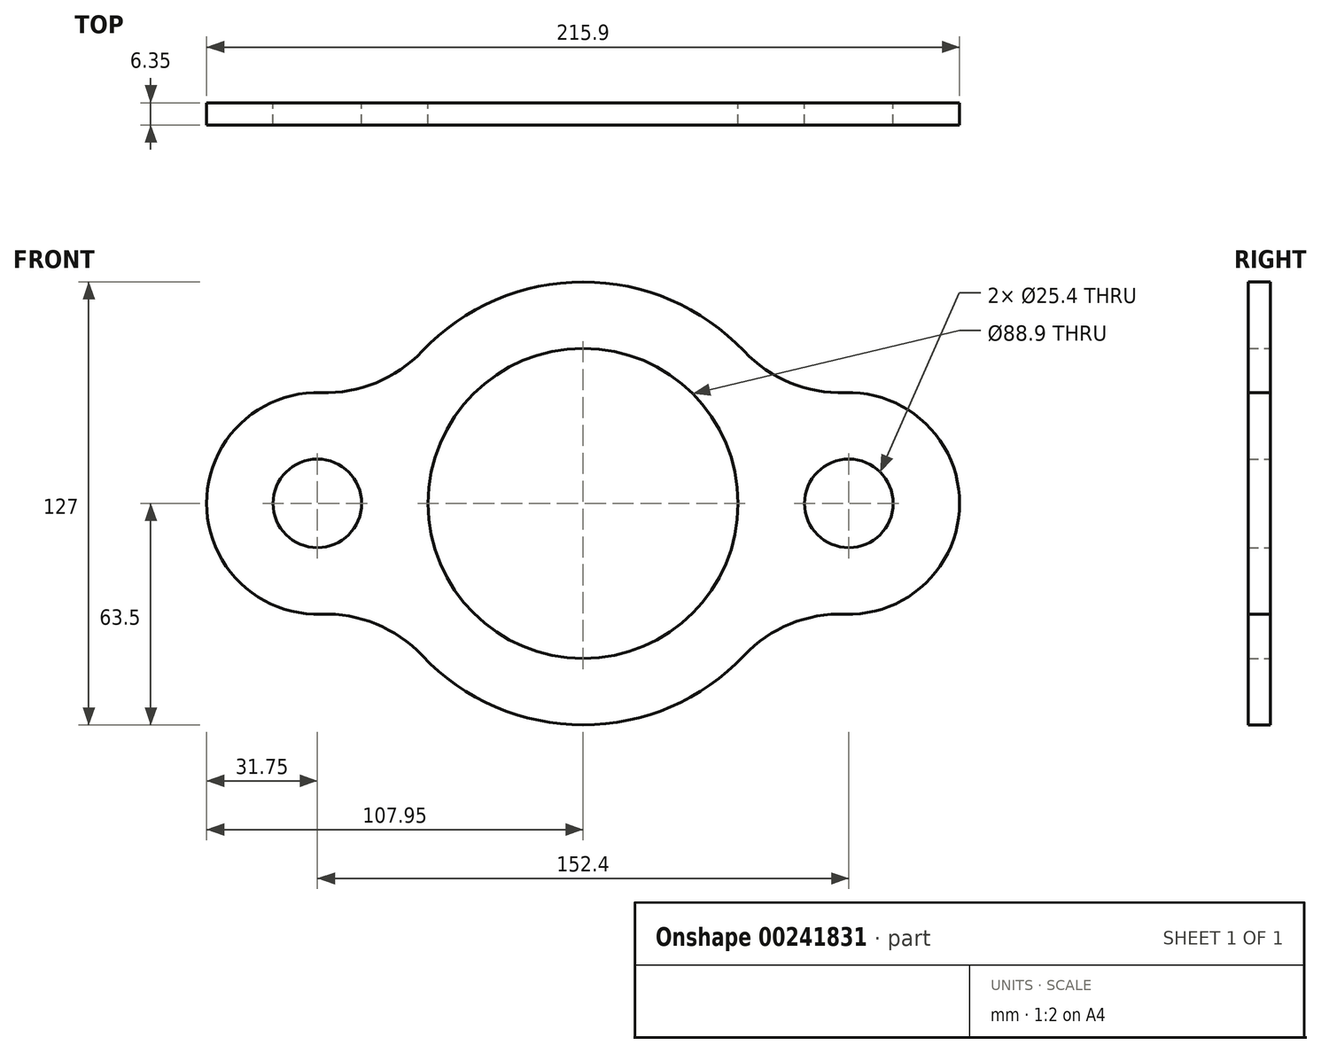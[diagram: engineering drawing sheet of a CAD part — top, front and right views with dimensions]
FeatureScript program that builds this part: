
annotation { "Feature Type Name" : "Feature", "Feature Type Description" : "" }
export const myFeature = defineFeature(function(context is Context, id is Id, definition is map)
    precondition{}
    {
        {
            var Q0;
            Q0=qCreatedBy(makeId("Front.planeOp"),FACE);
            var sketch = newSketch(context, id + "F0", { "sketchPlane" : qUnion([Q0])});
            skArc(sketch, "E0", {"start": v(-46.14, -43.63) * mm, "mid": v(0, -63.5) * mm, "end": v(46.14, -43.63) * mm});
            skCircle(sketch, "E1", {"center": v(0, 0) * mm, "radius": 44.45 * mm});
            skArc(sketch, "E2", {"start": v(75.12, -31.73) * mm, "mid": v(107.95, 0) * mm, "end": v(75.12, 31.73) * mm});
            skCircle(sketch, "E3", {"center": v(76.2, 0) * mm, "radius": 12.7 * mm});
            skArc(sketch, "E4", {"start": v(-75.12, 31.73) * mm, "mid": v(-107.95, 0) * mm, "end": v(-75.12, -31.73) * mm});
            skCircle(sketch, "E5", {"center": v(-76.2, 0) * mm, "radius": 12.7 * mm});
            skArc(sketch, "E6.trimOffspring", {"start": v(46.14, 43.63) * mm, "mid": v(0, 63.5) * mm, "end": v(-46.14, 43.63) * mm});
            skPoint(sketch, "E7.visualSharp", {"position": v(-57.94, 25.98) * mm});
            skArc(sketch, "E7.filletArc", {"start": v(-75.12, 31.73) * mm, "mid": v(-59.35, 34.56) * mm, "end": v(-46.14, 43.63) * mm});
            skPoint(sketch, "E8.visualSharp", {"position": v(57.94, 25.98) * mm});
            skArc(sketch, "E8.filletArc", {"start": v(46.14, 43.63) * mm, "mid": v(59.35, 34.56) * mm, "end": v(75.12, 31.73) * mm});
            skPoint(sketch, "E9.visualSharp", {"position": v(57.94, -25.98) * mm});
            skArc(sketch, "E9.filletArc", {"start": v(75.12, -31.73) * mm, "mid": v(59.35, -34.56) * mm, "end": v(46.14, -43.63) * mm});
            skPoint(sketch, "E10.visualSharp", {"position": v(-57.94, -25.98) * mm});
            skArc(sketch, "E10.filletArc", {"start": v(-46.14, -43.63) * mm, "mid": v(-59.35, -34.56) * mm, "end": v(-75.12, -31.73) * mm});
            skSolve(sketch);
        }
        {
            var Q0;
            Q0=makeQuery(id+"F0.imprint","IMPRINT",FACE,{"disambiguationData":[TD([[makeQuery(id+"F0.imprint","IMPRINT",EDGE,{"derivedFrom":sQuery(id+"F0.wireOp",EDGE,"E0")}),1.0]])]});
            extrude(context, id + "F1", {"entities" : qUnion([Q0]), "depth" : 6.35 * mm});
        }
    });
